FCSTD DOCUMENT  (FreeCAD 0.20R)
Label: our project
License: All rights reserved
LicenseURL: http://en.wikipedia.org/wiki/All_rights_reserved
objects: Sketcher::SketchObject×1, PartDesign::Body×1
note: 2 computed .brp shape members not serialized (recipe doc carries the construction recipe); baked Part::Feature solids carry a one-line shape summary decoded from their .brp

FEATURE [Sketcher::SketchObject] Sketch
  FullyConstrained = false
  MapMode = 5
  Placement = pos=(0,0,0) rot=(0.57735,0.57735,0.57735;2.0944rad)
  Support = -> [YZ_Plane]
  sketch-geometry (23):
    g0: LineSegment StartX=-137.619 StartY=-79.9142 StartZ=0 EndX=-17.6187 EndY=-79.9142 EndZ=0
    g1: LineSegment StartX=-17.6187 StartY=-79.9142 StartZ=0 EndX=-17.6187 EndY=-39.9142 EndZ=0
    g2: LineSegment StartX=-17.6187 StartY=-39.9142 StartZ=0 EndX=-57.6187 EndY=-39.9142 EndZ=0
    g3: LineSegment StartX=-57.6187 StartY=-39.9142 StartZ=0 EndX=-140.232 EndY=-59.9142 EndZ=0
    g4: LineSegment StartX=-140.232 StartY=-59.9142 StartZ=0 EndX=-137.619 EndY=-79.9142 EndZ=0
    g5: LineSegment StartX=58.7207 StartY=23.5183 StartZ=0 EndX=97.2879 EndY=30.3187 EndZ=0
    g6: LineSegment StartX=97.2879 StartY=30.3187 StartZ=0 EndX=97.2879 EndY=69.4809 EndZ=0
    g7: LineSegment StartX=97.2879 StartY=69.4809 StartZ=0 EndX=58.7207 EndY=23.5183 EndZ=0
    g8: LineSegment StartX=58.7207 StartY=23.5183 StartZ=0 EndX=-56.186 EndY=119.936 EndZ=0
    g9: LineSegment StartX=-56.186 StartY=119.936 StartZ=0 EndX=-17.6187 EndY=165.899 EndZ=0
    g10: LineSegment StartX=-17.6187 StartY=165.899 StartZ=0 EndX=97.2879 EndY=69.4809 EndZ=0
    g11: LineSegment StartX=-56.186 StartY=119.936 StartZ=0 EndX=-56.186 EndY=165.899 EndZ=0
    g12: LineSegment StartX=-56.186 StartY=165.899 StartZ=0 EndX=-17.6187 EndY=165.899 EndZ=0
    g13: LineSegment StartX=-17.6187 StartY=165.899 StartZ=0 EndX=-56.186 EndY=119.936 EndZ=0
    g14: LineSegment StartX=284.298 StartY=67.6192 StartZ=0 EndX=322.865 EndY=74.4196 EndZ=0
    g15: LineSegment StartX=322.865 StartY=74.4196 StartZ=0 EndX=322.865 EndY=113.582 EndZ=0
    g16: LineSegment StartX=322.865 StartY=113.582 StartZ=0 EndX=284.298 EndY=67.6192 EndZ=0
    g17: LineSegment StartX=284.298 StartY=67.6192 StartZ=0 EndX=169.391 EndY=164.037 EndZ=0
    g18: LineSegment StartX=169.391 StartY=164.037 StartZ=0 EndX=207.958 EndY=210 EndZ=0
    g19: LineSegment StartX=207.958 StartY=210 StartZ=0 EndX=322.865 EndY=113.582 EndZ=0
    g20: LineSegment StartX=169.391 StartY=164.037 StartZ=0 EndX=169.391 EndY=210 EndZ=0
    g21: LineSegment StartX=169.391 StartY=210 StartZ=0 EndX=207.958 EndY=210 EndZ=0
    g22: LineSegment StartX=207.958 StartY=210 StartZ=0 EndX=169.391 EndY=164.037 EndZ=0
  constraints (64):
    c: Horizontal(g0)
    c: Coincident(g0,g1)
    c: Vertical(g1)
    c: Coincident(g1,g2)
    c: Horizontal(g2)
    c: Coincident(g2,g3)
    c: Coincident(g3,g4)
    c: Coincident(g4,g0)
    c: DistanceX(g0,g0) = 120
    c: DistanceX(g2,g2) = 40
    c: DistanceY(g1,g1) = 40
    c: Distance(g3) = 85
    c: DistanceY(g4,g4) = 20
    c: Coincident(g5,g6)
    c: Vertical(g6)
    c: Coincident(g6,g7)
    c: Coincident(g7,g5)
    c: Angle(g5,g7) = 0.698132
    c: Angle(g7,g6) = 0.698132
    c: Coincident(g5,g8)
    c: Coincident(g8,g9)
    c: Coincident(g9,g10)
    c: Coincident(g10,g6)
    c: Distance(g10) = 150
    c: Angle(g10,g7) = 1.5708
    c: Angle(g7,g8) = 1.5708
    c: Distance(g8) = 150
    c: Distance(g7) = 60
    c: Coincident(g8,g11)
    c: Vertical(g11)
    c: Coincident(g11,g12)
    c: PointOnObject(g12,g9)
    c: Horizontal(g12)
    c: Coincident(g12,g13)
    c: Coincident(g13,g11)
    c: Angle(g9,g11) = 0.698132
    c: Angle(g12,g9) = 0.872665
    c: Distance(g9) = 60
    c: PointOnObject(g12,g1)
    c: PointOnObject(g9,g1)
    c: Coincident(g14,g15)
    c: Vertical(g15)
    c: Coincident(g15,g16)
    c: Coincident(g16,g14)
    c: Angle(g14,g16) = 0.698132
    c: Angle(g16,g15) = 0.698132
    c: Coincident(g14,g17)
    c: Coincident(g17,g18)
    c: Coincident(g18,g19)
    c: Coincident(g19,g15)
    c: Equal(g10,g19) = 150
    c: Angle(g19,g16) = 1.5708
    c: Angle(g16,g17) = 1.5708
    c: Equal(g8,g17) = 150
    c: Equal(g7,g16) = 60
    c: Coincident(g17,g20)
    c: Vertical(g20)
    c: Coincident(g20,g21)
    c: PointOnObject(g21,g18)
    c: Horizontal(g21)
    c: Coincident(g21,g22)
    c: Coincident(g22,g20)
    c: Angle(g18,g20) = 0.698132
    c: Angle(g21,g18) = 0.872665
FEATURE [PartDesign::Body] Body
  Group = -> [Sketch]
  Origin = -> Origin
